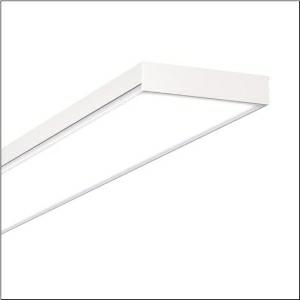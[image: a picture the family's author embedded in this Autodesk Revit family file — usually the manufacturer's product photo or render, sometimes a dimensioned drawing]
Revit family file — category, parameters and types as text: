
# Revit family: apollon_31_surface_51mp26wd2441wa
name_source: partatom
category: Lighting Fixtures
units: mm (PartAtom-declared; Revit-internal decimal feet)

## family parameters
Cut with Voids When Loaded = No
Host = Face
Light Source = No
Part Type = Normal
Room Calculation Point = No
Round Connector Dimension = Use Diameter
Shared = No

## types (1)
- Apollon 31 Surface (1 x LED, 4600 lm, 33 W, 4000K)
    Apparent Load = 33 VA
    CIE Flux Codes = 61 87 97 97 100
    Color Rendering = 80
    Color Temperature = 4000K
    Default Elevation = 1800 mm
    Description = Apollon 31 Surface, office luminaire, primary optical cover: micro prismatic cover, of PMMA, light emission: direct distribution, primary light characteristic: symmetric, installation type: surface-mounted, LED, rated luminous flux: 4.600lm, luminous efficacy: 139lm/W, light colour: 840, colour temperature: 4000K, control gear: DALI 2, with terminal, 5-pole, mains connection: 220..240V, AC, 50/60Hz, rated input power: 33W, housing, of sheet steel, coated, traffic white (RAL 9016), length: 1.545mm, width: 200mm, height: 44mm, protection rating (complete): IP20, protection rating (on room side): IP40, protection rating (lamp compartment, on room side): IP40, insulation class (complete): insulation class I (protective earthing), certification: CE, ENEC, UKCA, impact resistance: IK02, permissible operating ambient temperature: -20..+40°C, standard: EN 60598-2-22, packaging unit: 1 piece
    Height = 44 mm
    Lamp = 1 x LED
    Lamp Light Flux = 4600 lm
    Lamp Power = 33 W
    Lamp count = 1
    Length = 1545 mm
    Luminous efficacy = 139 lm/W
    Manufacturer = Siteco
    ModVariant = No
    Model = 51MP26WD2441WA
    Mounting Place = Ceiling
    Mounting Type = Surface mounted
    Number of Poles = 1
    OnlyDefault = Yes
    Power Factor = 1
    Product Name = Apollon 31 Surface
    Product group = office luminaire | ceiling mounted
    ProductGroupID = 301
    Protection Class = Protection class I
    Protection Degree = IP 20
    RLX_Detail_Level = 1
    RLX_Emergency_Light_Flux = 0 lm
    RLX_Emergency_Type = 0
    RLX_Emergency_Type_DB = No
    RlxData = <blob elided: 20809 chars, md5=b398f78f>
    Socket = socket
    Standby Power = 0 W
    System Light Flux = 4600 lm
    System Power = 33 W
    Type Comments = Product without accessories
    Type Image = l_1313658.jpg
    URL = http://relux.com
    VarID = ---
    Voltage = 0 V
    Weight = 0.00 kg
    Width = 200 mm  [stored 0.656168 ft]

note: [stored X ft] marks values corroborated as IEEE doubles in the binary element streams (Revit-internal decimal feet)

## geometry (parser evidence)
native form markers: Blend x4, Sweep x10
no freeform markers — native parametric forms only
